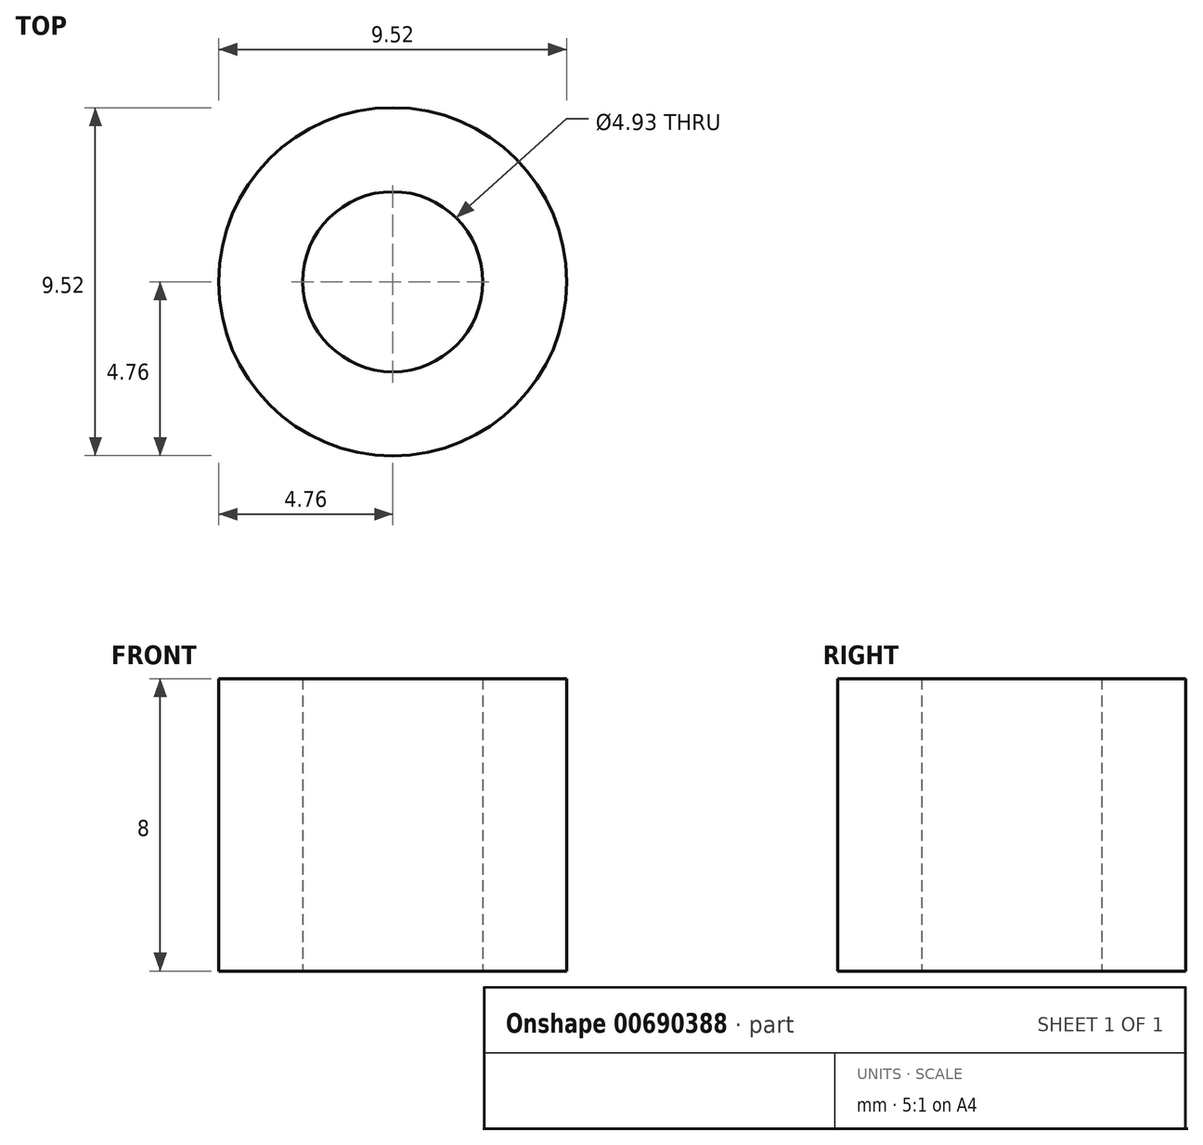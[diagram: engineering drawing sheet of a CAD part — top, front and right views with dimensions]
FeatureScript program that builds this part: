
annotation { "Feature Type Name" : "Feature", "Feature Type Description" : "" }
export const myFeature = defineFeature(function(context is Context, id is Id, definition is map)
    precondition{}
    {
        {
            var Q0;
            Q0=qCreatedBy(makeId("Top.planeOp"),FACE);
            var sketch = newSketch(context, id + "F0", { "sketchPlane" : qUnion([Q0])});
            skCircle(sketch, "E0", {"center": v(0, 0) * mm, "radius": 4.76 * mm});
            skCircle(sketch, "E1", {"center": v(0, 0) * mm, "radius": 2.46 * mm});
            skSolve(sketch);
        }
        {
            var Q0;
            Q0 = qSketchRegion(id + "F0", true);
            extrude(context, id + "F1", {"entities" : qUnion([Q0]), "depth" : 8 * mm, "offsetDistance" : 25.4 * mm});
        }
    });
